# Revit family: 2.rvt
name_source: partatom
category: Pipe Accessories
revit_build: Autodesk Revit 2018 (Build: 20190510_1515(x64)
units: mm (PartAtom-declared; Revit-internal decimal feet)

## family parameters
Always vertical = No
Cut with Voids When Loaded = No
OmniClass Number = 23.65.00.00
OmniClass Title = Supply and Distribution of Liquids and Gases
Part Type = Normal
Round Connector Dimension = Use Diameter
Shared = No
Work Plane-Based = No

## types (2) — shared parameters
Antifreeze: = Passiveted Propylene Glycol
Application fluids = Water or glycol solutions
BIMobject category = HVAC: Other HVAC
Body Material = Pintossi - Metal - Brass CW617N
Brand url = http://www.pintossi.it
Conditioning: = as indicated by the producer
Copper (CU): = < 0,1 mg/kg (< 0,05 mg/kg for steam)
Description = Pintossi+C motorized zone valves are the perfect solution to be used when a thermal regulation divided in more enviroments is needed, connecting the valve to a room thermostat, giving the information of opening/closing, depending on the set temperature.

Pintossi+C zone valves garantuee high performance levels: reduced dimensions and ease of use during installation allow to automatically intercept the fluid in hydraulic water systems and zone heating systems.

Besides the valve is equipped with APS (Anti-locking Pintossi System) a unique patented mechanism which prevent the opening and closing operation locking caused by dirt and limescale.

All the valves are equipped with pipe unions for an easy installation.

Main features:

- No seepage

- Short opening and closing times

- Operational capacity with high differential pressures

- Low head losses thanks to the full bore flow

- Match with any type of 3-contact controls

The valve can be easily motorized using Pintossi+C actuator art.770 that can be used even with manual option.
Design country = Italy
Edition number = 1
Fluid aspect: = Limpid
IFC Classification = Valve
Iron (FE): = < 0,5 mg/kg (< 0,1 mg/kg for steam)
Manufacturer = Pintossi+c
Manufacturer country = Italy
Manufacturer name = Pintossi+c
Masterformat 2014 Code = 23 00 00
Masterformat 2014 Description = Heating, Ventilating, and Air Conditioning (HVAC)
Material main = Brass
Maximum percentage of glycol [%] = 30
Maximum working pressure = 1000000.0 Pa
Maximum working temperature = 110 °C
Model = 772
NBS Reference Code = 94-94
NBS Reference Description = Valves
OmniClass Code = 23-27 31 00
OmniClass Description = Valves
PH: = Between 7 and 8Between 7 and 8
Product Guid = 7d02ca70-db8c-4f84-983d-8de72317b0d6
Product data url = https://www.bimobject.com
Product family = Zone valves
Product group = Ball zone valves
Protection level = 90.00°
Rotation angle = -10÷55°C
Torque = 800 mm  [stored 2.62467 ft]
UNSPSC Code = 401416
URL = www.pintossi.it
Uniclass 1.4 Code = L7136
Uniclass 1.4 Description = Valves
Uniclass 2.0 Code = PR-94
Uniclass 2.0 Description = Valves
Uniclass 2015 Code = Ss_60
Uniclass 2015 Name = Heating, cooling and refrigeration systems
Uniformat II Code = D30
Uniformat II Description = HVAC
Voltage = 230 V

## per-type parameters (varying)
| type | Main Inlet/Outlet 1" | Main Inlet/Outlet 3/4" | Main Inlet/Outlet Diameter | Main Inlet/Outlet Radius | Mainfold Length |
| 1" - 2 ways | Yes | No | 25 mm  [stored 0.082021 ft] | 13 mm | 145 mm  [stored 0.475722 ft] |
| 3/4" - 2 ways | No | Yes | 19 mm | 10 mm  [stored 0.0328084 ft] | 130 mm  [stored 0.426509 ft] |

note: [stored X ft] marks values corroborated as IEEE doubles in the binary element streams (Revit-internal decimal feet)

## geometry (parser evidence)
native form markers: Sweep x1
no freeform markers — native parametric forms only
